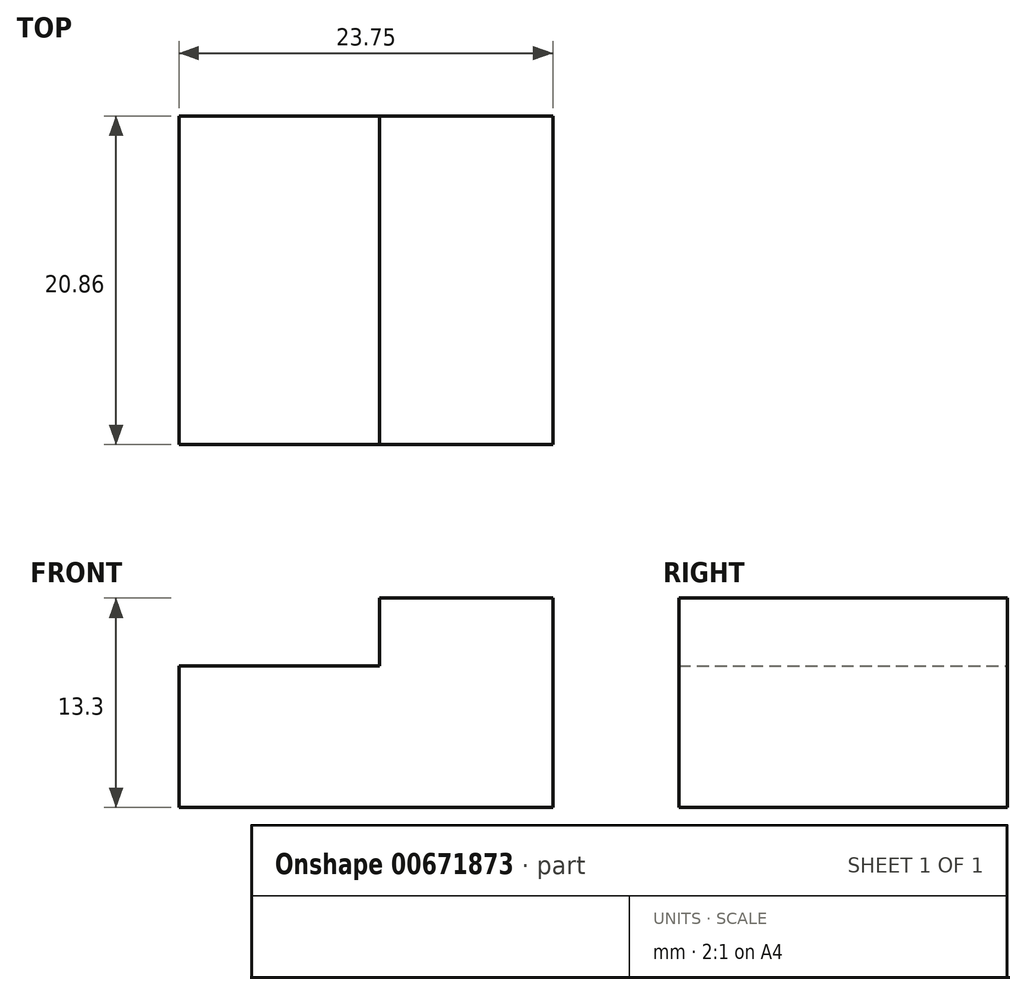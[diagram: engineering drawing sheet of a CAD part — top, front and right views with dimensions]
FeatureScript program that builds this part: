
annotation { "Feature Type Name" : "Feature", "Feature Type Description" : "" }
export const myFeature = defineFeature(function(context is Context, id is Id, definition is map)
    precondition{}
    {
        {
            var Q0;
            Q0=qCreatedBy(makeId("Front.planeOp"),FACE);
            var sketch = newSketch(context, id + "F0", { "sketchPlane" : qUnion([Q0])});
            skLineSegment(sketch, "E0", {"start": v(0, 0) * mm, "end": v(23.75, 0) * mm});
            skLineSegment(sketch, "E1", {"start": v(23.75, 0) * mm, "end": v(23.75, 13.3) * mm});
            skLineSegment(sketch, "E2", {"start": v(23.75, 13.3) * mm, "end": v(12.75, 13.3) * mm});
            skLineSegment(sketch, "E3", {"start": v(12.75, 13.3) * mm, "end": v(12.75, 9) * mm});
            skLineSegment(sketch, "E4", {"start": v(12.75, 9) * mm, "end": v(0, 9) * mm});
            skLineSegment(sketch, "E5", {"start": v(0, 9) * mm, "end": v(0, 0) * mm});
            skSolve(sketch);
        }
        {
            var Q0;
            Q0=makeQuery(id+"F0.imprint","IMPRINT",FACE,{"disambiguationData":[TD([[makeQuery(id+"F0.imprint","IMPRINT",EDGE,{"derivedFrom":sQuery(id+"F0.wireOp",EDGE,"E0")}),1.0]])]});
            extrude(context, id + "F1", {"entities" : qUnion([Q0]), "endBound" : BoundingType.SYMMETRIC, "depth" : 20.86 * mm, "offsetDistance" : 25 * mm});
        }
    });
